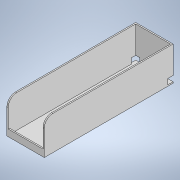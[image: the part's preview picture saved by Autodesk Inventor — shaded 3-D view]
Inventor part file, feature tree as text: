
AUTODESK INVENTOR PART (.ipt)
format: ipt  version: 2022 (Build 260153000, 153)  size: 215,552 bytes
history: native  units: mm
features: extrude x10, sketch x10, fillet x2
ambient origin geometry x8: Origin, YZ Plane, XZ Plane, XY Plane, X Axis, Y Axis, Z Axis, Center Point
bodies: Solid1 (feature_tree)
feature tree (22):
  extrude  "Extrusion1"  Depth=15.7mm
  extrude  "Extrusion2"  Depth=3.0mm TaperAngle=0.0deg
  extrude  "Extrusion3"  Depth=3.0mm TaperAngle=0.0deg
  fillet  "Fillet1"  Radius=63.5mm
  extrude  "Extrusion4"  Depth=20.0mm
  fillet  "Fillet2"  Radius=63.5mm
  extrude  "Extrusion5"  Depth=3.0mm TaperAngle=0.0deg
  extrude  "Extrusion6"  Depth=3.0mm TaperAngle=0.0deg
  extrude  "Extrusion7"  Depth=12.515mm
  extrude  "Extrusion8"  Depth=3.0mm TaperAngle=0.0deg
  extrude  "Extrusion9"  Depth=3.0mm TaperAngle=0.0deg
  extrude  "Extrusion10"  Depth=12.515mm
  sketch  "Sketch1"  dims[d0=87.28mm d1=15.7mm]
  sketch  "Sketch2"  dims[d2=15.7mm d3=3.0mm d4=0.0mm]
  sketch  "Sketch3"  dims[d5=297.64mm d6=3.0mm d7=0.0mm d8=63.5mm]
  sketch  "Sketch4"  dims[d9=3.0mm d10=0.0mm d11=20.0mm d12=63.5mm]
  sketch  "Sketch5"  dims[d13=3.0mm d14=3.0mm d15=0.0mm]
  sketch  "Sketch6"  dims[d16=20.0mm d17=3.0mm d18=0.0mm]
  sketch  "Sketch7"  dims[d19=3.0mm d20=12.515mm]
  sketch  "Sketch8"  dims[d21=12.7mm d22=3.0mm d23=0.0mm]
  sketch  "Sketch9"  dims[d24=9.515mm d25=3.0mm d26=0.0mm]
  sketch  "Sketch10"  dims[d27=3.0mm d28=12.515mm d29=12.7mm d30=3.0mm d31=0.0mm d32=3.0mm d33=0.0mm d34=4.25mm d35=4.25mm d36=4.25mm d37=4.25mm d38=10.0mm d39=10.0mm d40=10.0mm d41=10.0mm d42=10.0mm d43=10.0mm d44=10.0mm d45=10.0mm d46=3.0mm d47=0.0mm]
